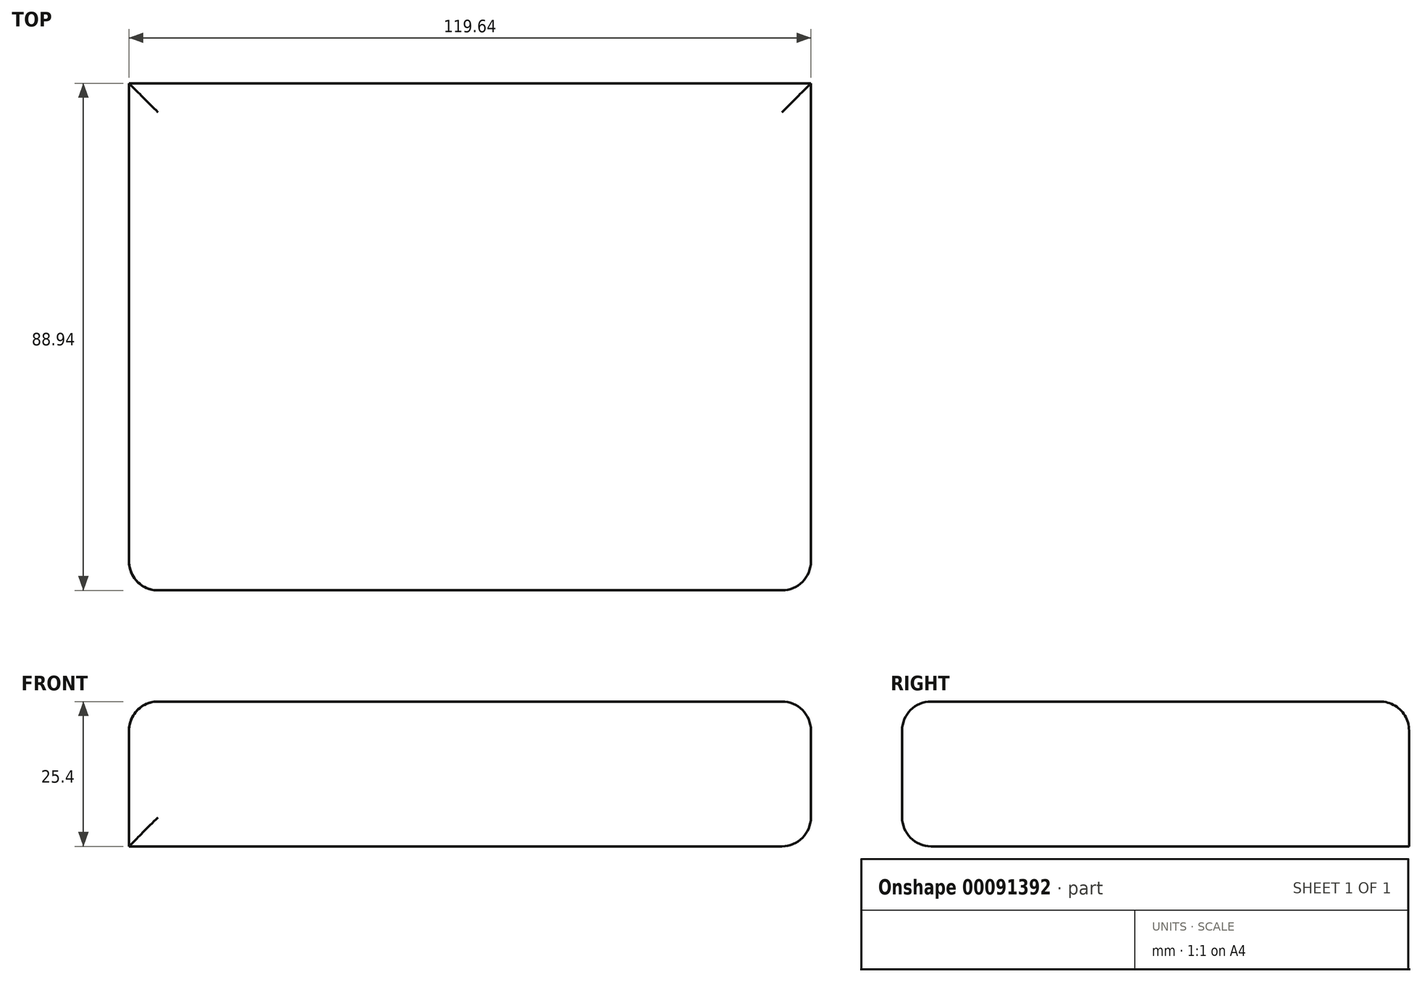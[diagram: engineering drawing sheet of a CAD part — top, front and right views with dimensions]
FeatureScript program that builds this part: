
annotation { "Feature Type Name" : "Feature", "Feature Type Description" : "" }
export const myFeature = defineFeature(function(context is Context, id is Id, definition is map)
    precondition{}
    {
        {
            var Q0;
            Q0=qCreatedBy(makeId("Top.planeOp"),FACE);
            var sketch = newSketch(context, id + "F0", { "sketchPlane" : qUnion([Q0])});
            skLineSegment(sketch, "E0.bottom", {"start": v(-93.72, 57.37) * mm, "end": v(25.92, 57.37) * mm});
            skLineSegment(sketch, "E0.top", {"start": v(-93.72, -31.57) * mm, "end": v(25.92, -31.57) * mm});
            skLineSegment(sketch, "E0.left", {"start": v(-93.72, 57.37) * mm, "end": v(-93.72, -31.57) * mm});
            skLineSegment(sketch, "E0.right", {"start": v(25.92, 57.37) * mm, "end": v(25.92, -31.57) * mm});
            skSolve(sketch);
        }
        {
            var Q0;
            Q0=makeQuery(id+"F0.imprint","IMPRINT",FACE,{"disambiguationData":[TD([[makeQuery(id+"F0.imprint","IMPRINT",EDGE,{"derivedFrom":sQuery(id+"F0.wireOp",EDGE,"E0.bottom")}),-1.0]])]});
            extrude(context, id + "F1", {"entities" : qUnion([Q0]), "depth" : 25.4 * mm});
        }
        {
            var Q0;
            Q0=makeQuery(id+"F1.opExtrude","CAP_EDGE",EDGE,{"disambiguationData":[OSD([sQuery(id+"F0.wireOp",EDGE,"E0.top")])],"isStart":false});
            var Q1;
            Q1=makeQuery(id+"F1.opExtrude","CAP_EDGE",EDGE,{"disambiguationData":[OSD([sQuery(id+"F0.wireOp",EDGE,"E0.left")])],"isStart":false});
            var Q2;
            Q2=makeQuery(id+"F1.opExtrude","CAP_EDGE",EDGE,{"disambiguationData":[OSD([sQuery(id+"F0.wireOp",EDGE,"E0.right")])],"isStart":false});
            var Q3;
            Q3=makeQuery(id+"F1.opExtrude","CAP_EDGE",EDGE,{"disambiguationData":[OSD([sQuery(id+"F0.wireOp",EDGE,"E0.bottom")])],"isStart":false});
            var Q4;
            Q4=makeQuery(id+"F1.opExtrude","SWEPT_EDGE",EDGE,{"disambiguationData":[OSD([sQuery(id+"F0.wireOp",EDGE,"E0.top"),sQuery(id+"F0.wireOp",EDGE,"E0.right")])]});
            var Q5;
            Q5=makeQuery(id+"F1.opExtrude","CAP_EDGE",EDGE,{"disambiguationData":[OSD([sQuery(id+"F0.wireOp",EDGE,"E0.right")])],"isStart":true});
            var Q6;
            Q6=makeQuery(id+"F1.opExtrude","CAP_EDGE",EDGE,{"disambiguationData":[OSD([sQuery(id+"F0.wireOp",EDGE,"E0.top")])],"isStart":true});
            var Q7;
            Q7=makeQuery(id+"F1.opExtrude","SWEPT_EDGE",EDGE,{"disambiguationData":[OSD([sQuery(id+"F0.wireOp",EDGE,"E0.top"),sQuery(id+"F0.wireOp",EDGE,"E0.left")])]});
            fillet(context, id + "F2", {"entities" : qUnion([Q0, Q1, Q2, Q3, Q4, Q5, Q6, Q7]), "radius" : 5.08 * mm, "tangentPropagation" : true, "allowEdgeOverflow" : false});
        }
    });
